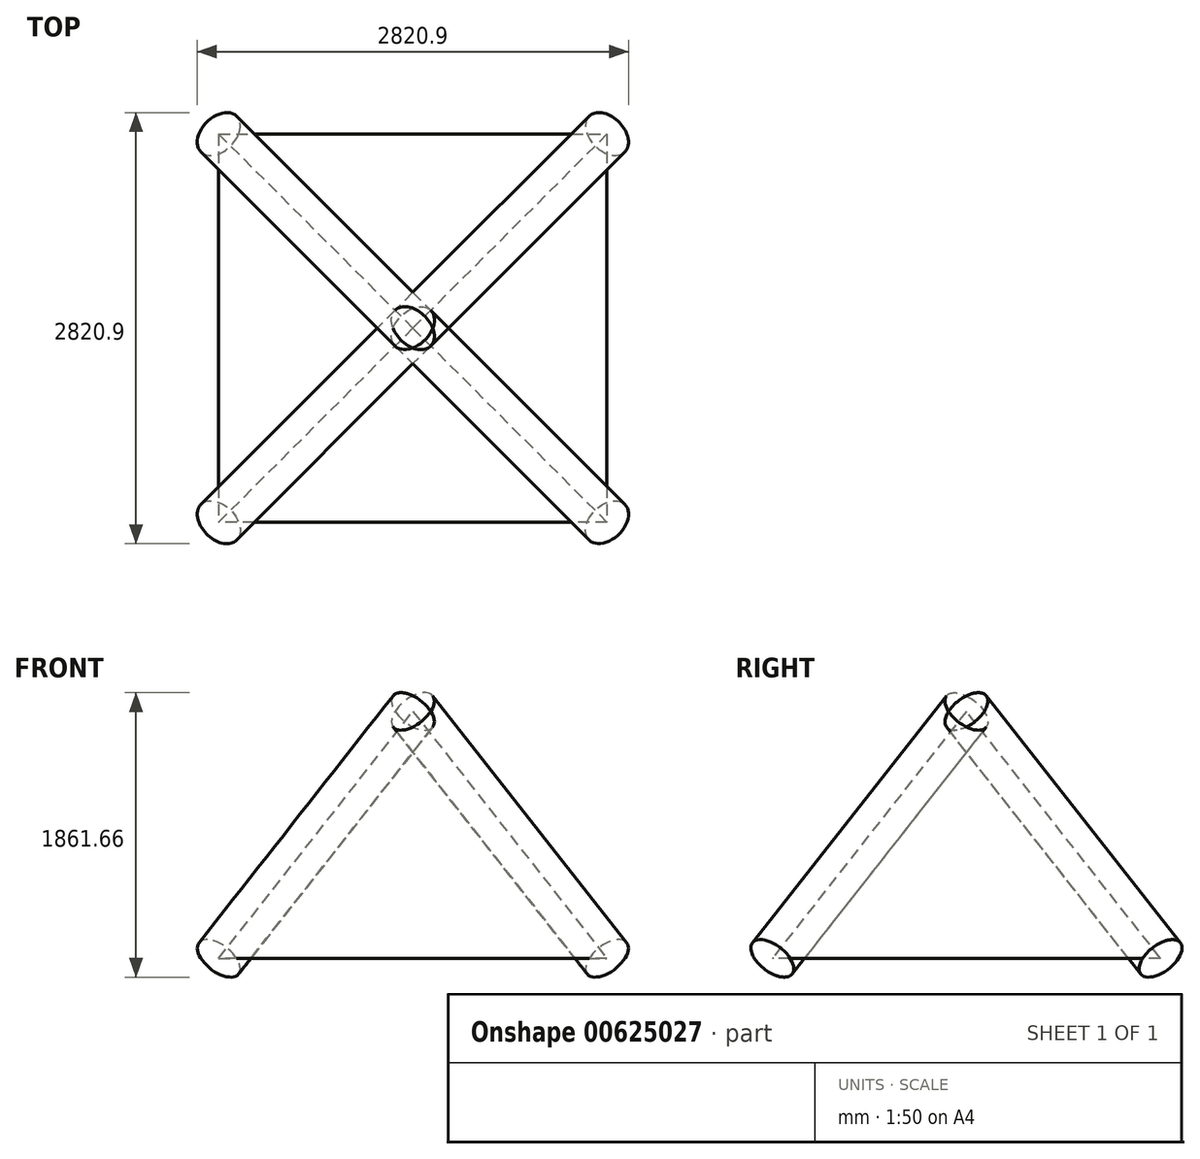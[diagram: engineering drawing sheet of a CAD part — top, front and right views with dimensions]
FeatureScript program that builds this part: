
annotation { "Feature Type Name" : "Feature", "Feature Type Description" : "" }
export const myFeature = defineFeature(function(context is Context, id is Id, definition is map)
    precondition{}
    {
        {
            var Q0;
            Q0=qCreatedBy(makeId("Front.planeOp"),FACE);
            var sketch = newSketch(context, id + "F0", { "sketchPlane" : qUnion([Q0])});
            skLineSegment(sketch, "E0", {"start": v(0, 0) * mm, "end": v(-2540, 0) * mm});
            skLineSegment(sketch, "E1", {"start": v(-2540, 0) * mm, "end": v(-1270, 1616.2) * mm});
            skLineSegment(sketch, "E2", {"start": v(-1270, 1616.2) * mm, "end": v(0, 0) * mm});
            skSolve(sketch);
        }
        {
            var Q0;
            Q0 = qSketchRegion(id + "F0", true);
            extrude(context, id + "F1", {"entities" : qUnion([Q0]), "oppositeDirection" : true, "depth" : 3048 * mm, "offsetDistance" : 25.4 * mm});
        }
        {
            var Q0;
            Q0=qCreatedBy(makeId("Right.planeOp"),FACE);
            var sketch = newSketch(context, id + "F2", { "sketchPlane" : qUnion([Q0])});
            skLineSegment(sketch, "E3", {"start": v(0, 0) * mm, "end": v(2540, 0) * mm});
            skLineSegment(sketch, "E4", {"start": v(2540, 0) * mm, "end": v(1270, 1616.2) * mm});
            skLineSegment(sketch, "E5", {"start": v(0, 0) * mm, "end": v(1270, 1616.2) * mm});
            skSolve(sketch);
        }
        {
            var Q0;
            Q0 = qSketchRegion(id + "F2", true);
            extrude(context, id + "F3", {"entities" : qUnion([Q0]), "operationType" : NewBodyOperationType.INTERSECT, "oppositeDirection" : true, "depth" : 2794 * mm, "offsetDistance" : 25.4 * mm});
        }
        {
            var Q0;
            Q0=makeQuery(id+"F1.opExtrude","SWEPT_FACE",FACE,{"disambiguationData":[OSD([sQuery(id+"F0.wireOp",EDGE,"E2")])]});
            var sketch = newSketch(context, id + "F4", { "sketchPlane" : qUnion([Q0])});
            skLineSegment(sketch, "E6", {"start": v(0, 0) * mm, "end": v(1270, 2055.48) * mm});
            skLineSegment(sketch, "E7.0", {"start": v(140.45, -86.78) * mm, "end": v(1410.45, 1968.7) * mm});
            skLineSegment(sketch, "E8.1", {"start": v(6.35, 22.36) * mm, "end": v(1254.72, 2042.84) * mm});
            skLineSegment(sketch, "E9", {"start": v(0, 0) * mm, "end": v(140.45, -86.78) * mm});
            skLineSegment(sketch, "E10", {"start": v(1410.45, 1968.7) * mm, "end": v(1270, 2055.48) * mm});
            skSolve(sketch);
        }
        {
            var Q0;
            Q0 = qSketchRegion(id + "F4", true);
            var Q1;
            Q1=sQuery(id+"F4.wireOp",EDGE,"E6");
            revolve(context, id + "F5", {"entities" : qUnion([Q0]), "axis" : qUnion([Q1]), "revolveType" : RevolveType.FULL});
        }
        {
            var Q0;
            Q0=makeQuery(id+"F1.opExtrude","SWEPT_FACE",FACE,{"disambiguationData":[OSD([sQuery(id+"F0.wireOp",EDGE,"E2")])]});
            var sketch = newSketch(context, id + "F6", { "sketchPlane" : qUnion([Q0])});
            skLineSegment(sketch, "E11", {"start": v(1270, 2055.48) * mm, "end": v(2540, 0) * mm});
            skLineSegment(sketch, "E12.0", {"start": v(1410.45, 2142.26) * mm, "end": v(2680.45, 86.78) * mm});
            skLineSegment(sketch, "E13", {"start": v(1270, 2055.48) * mm, "end": v(1410.45, 2142.26) * mm});
            skLineSegment(sketch, "E14", {"start": v(2540, 0) * mm, "end": v(2680.45, 86.78) * mm});
            skSolve(sketch);
        }
        {
            var Q0;
            Q0 = qSketchRegion(id + "F6", true);
            var Q1;
            Q1=sQuery(id+"F6.wireOp",EDGE,"E11");
            revolve(context, id + "F7", {"entities" : qUnion([Q0]), "axis" : qUnion([Q1]), "revolveType" : RevolveType.FULL});
        }
        {
            var Q0;
            Q0=makeQuery(id+"F1.opExtrude","SWEPT_FACE",FACE,{"disambiguationData":[OSD([sQuery(id+"F0.wireOp",EDGE,"E1")])]});
            var sketch = newSketch(context, id + "F8", { "sketchPlane" : qUnion([Q0])});
            skLineSegment(sketch, "E15", {"start": v(0, -1569.36) * mm, "end": v(-1270, 486.12) * mm});
            skLineSegment(sketch, "E16.0", {"start": v(-140.45, -1656.14) * mm, "end": v(-1410.45, 399.34) * mm});
            skLineSegment(sketch, "E17", {"start": v(0, -1569.36) * mm, "end": v(-140.45, -1656.14) * mm});
            skLineSegment(sketch, "E18", {"start": v(-1270, 486.12) * mm, "end": v(-1410.45, 399.34) * mm});
            skSolve(sketch);
        }
        {
            var Q0;
            Q0 = qSketchRegion(id + "F8", true);
            var Q1;
            Q1=sQuery(id+"F8.wireOp",EDGE,"E15");
            revolve(context, id + "F9", {"entities" : qUnion([Q0]), "axis" : qUnion([Q1]), "revolveType" : RevolveType.FULL});
        }
        {
            var Q0;
            Q0=makeQuery(id+"F1.opExtrude","SWEPT_FACE",FACE,{"disambiguationData":[OSD([sQuery(id+"F0.wireOp",EDGE,"E1")])]});
            var sketch = newSketch(context, id + "F10", { "sketchPlane" : qUnion([Q0])});
            skLineSegment(sketch, "E19", {"start": v(-1270, 486.12) * mm, "end": v(-2540, -1569.36) * mm});
            skLineSegment(sketch, "E20.0", {"start": v(-1410.45, 572.9) * mm, "end": v(-2680.45, -1482.58) * mm});
            skLineSegment(sketch, "E21", {"start": v(-1410.45, 572.9) * mm, "end": v(-1270, 486.12) * mm});
            skLineSegment(sketch, "E22", {"start": v(-2540, -1569.36) * mm, "end": v(-2680.45, -1482.58) * mm});
            skSolve(sketch);
        }
        {
            var Q0;
            Q0 = qSketchRegion(id + "F10", true);
            var Q1;
            Q1=sQuery(id+"F10.wireOp",EDGE,"E19");
            revolve(context, id + "F11", {"entities" : qUnion([Q0]), "axis" : qUnion([Q1]), "revolveType" : RevolveType.FULL});
        }
    });
